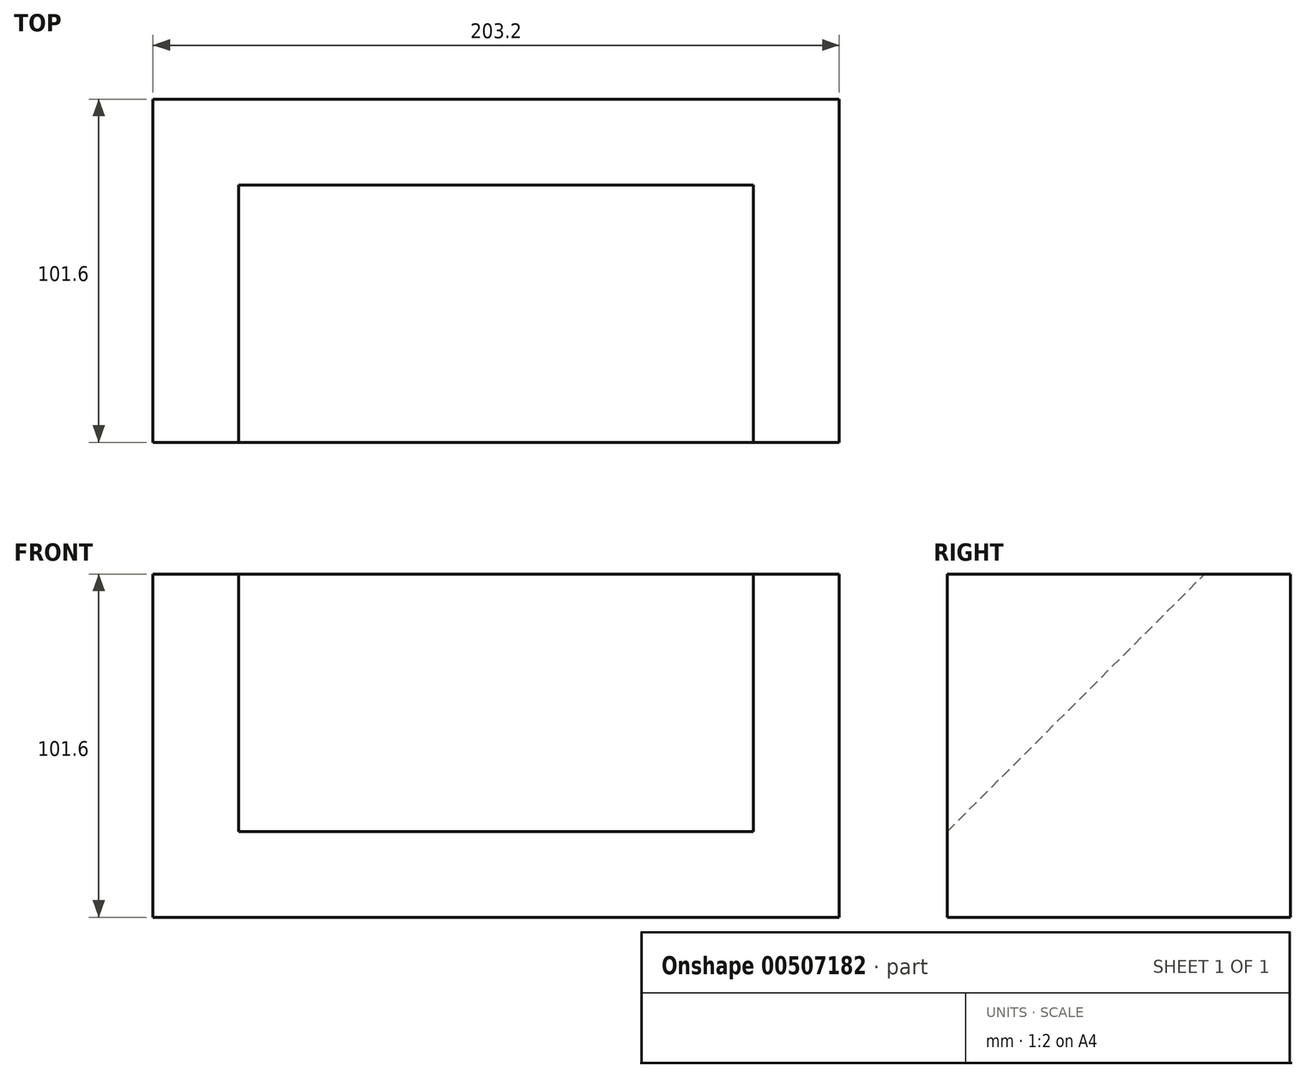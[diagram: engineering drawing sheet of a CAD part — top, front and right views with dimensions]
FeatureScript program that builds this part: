
annotation { "Feature Type Name" : "Feature", "Feature Type Description" : "" }
export const myFeature = defineFeature(function(context is Context, id is Id, definition is map)
    precondition{}
    {
        {
            var Q0;
            Q0=qCreatedBy(makeId("Top.planeOp"),FACE);
            var sketch = newSketch(context, id + "F0", { "sketchPlane" : qUnion([Q0])});
            skLineSegment(sketch, "E0.bottom", {"start": v(0, 0) * mm, "end": v(203.2, 0) * mm});
            skLineSegment(sketch, "E0.top", {"start": v(0, -101.6) * mm, "end": v(203.2, -101.6) * mm});
            skLineSegment(sketch, "E0.left", {"start": v(0, 0) * mm, "end": v(0, -101.6) * mm});
            skLineSegment(sketch, "E0.right", {"start": v(203.2, 0) * mm, "end": v(203.2, -101.6) * mm});
            skSolve(sketch);
        }
        {
            var Q0;
            Q0=makeQuery(id+"F0.imprint","IMPRINT",FACE,{"disambiguationData":[TD([[makeQuery(id+"F0.imprint","IMPRINT",EDGE,{"derivedFrom":sQuery(id+"F0.wireOp",EDGE,"E0.bottom")}),-1.0]])]});
            var sketch = newSketch(context, id + "F1", { "sketchPlane" : qUnion([Q0])});
            skLineSegment(sketch, "E1.bottom", {"start": v(25.4, -101.6) * mm, "end": v(177.8, -101.6) * mm});
            skLineSegment(sketch, "E1.top", {"start": v(25.4, -25.4) * mm, "end": v(177.8, -25.4) * mm});
            skLineSegment(sketch, "E1.left", {"start": v(25.4, -101.6) * mm, "end": v(25.4, -25.4) * mm});
            skLineSegment(sketch, "E1.right", {"start": v(177.8, -101.6) * mm, "end": v(177.8, -25.4) * mm});
            skSolve(sketch);
        }
        {
            var Q0;
            Q0=makeQuery(id+"F1.imprint","IMPRINT",FACE,{"disambiguationData":[TD([[makeQuery(id+"F1.imprint","IMPRINT",EDGE,{"derivedFrom":sQuery(id+"F1.wireOp",EDGE,"E1.bottom")}),1.0]])]});
            extrude(context, id + "F2", {"entities" : qUnion([Q0]), "depth" : 101.6 * mm});
        }
        {
            var Q0;
            Q0=makeQuery(id+"F2.opExtrude","CAP_EDGE",EDGE,{"disambiguationData":[OSD([sQuery(id+"F1.wireOp",EDGE,"E1.bottom")])],"isStart":false});
            chamfer(context, id + "F3", {"entities" : qUnion([Q0]), "chamferType" : ChamferType.TWO_OFFSETS, "width1" : 76.2 * mm, "oppositeDirection" : false, "width2" : 76.2 * mm, "tangentPropagation" : true});
        }
        {
            var Q0;
            Q0=makeQuery(id+"F0.imprint","IMPRINT",FACE,{"disambiguationData":[TD([[makeQuery(id+"F0.imprint","IMPRINT",EDGE,{"derivedFrom":sQuery(id+"F0.wireOp",EDGE,"E0.bottom")}),-1.0]])]});
            var sketch = newSketch(context, id + "F4", { "sketchPlane" : qUnion([Q0])});
            skLineSegment(sketch, "E2", {"start": v(0, 0) * mm, "end": v(0, -101.6) * mm});
            skLineSegment(sketch, "E3", {"start": v(0, -101.6) * mm, "end": v(25.4, -101.6) * mm});
            skLineSegment(sketch, "E4", {"start": v(25.4, -101.6) * mm, "end": v(25.4, -25.4) * mm});
            skLineSegment(sketch, "E5", {"start": v(25.4, -25.4) * mm, "end": v(177.8, -25.4) * mm});
            skLineSegment(sketch, "E6", {"start": v(177.8, -25.4) * mm, "end": v(177.8, -101.6) * mm});
            skLineSegment(sketch, "E7", {"start": v(177.8, -101.6) * mm, "end": v(203.2, -101.6) * mm});
            skLineSegment(sketch, "E8", {"start": v(203.2, -101.6) * mm, "end": v(203.2, 0) * mm});
            skLineSegment(sketch, "E9", {"start": v(203.2, 0) * mm, "end": v(0, 0) * mm});
            skSolve(sketch);
        }
        {
            var Q0;
            Q0=makeQuery(id+"F4.imprint","IMPRINT",FACE,{"disambiguationData":[TD([[makeQuery(id+"F4.imprint","IMPRINT",EDGE,{"derivedFrom":sQuery(id+"F4.wireOp",EDGE,"E2")}),1.0]])]});
            extrude(context, id + "F5", {"entities" : qUnion([Q0]), "operationType" : NewBodyOperationType.ADD, "depth" : 101.6 * mm});
        }
    });
